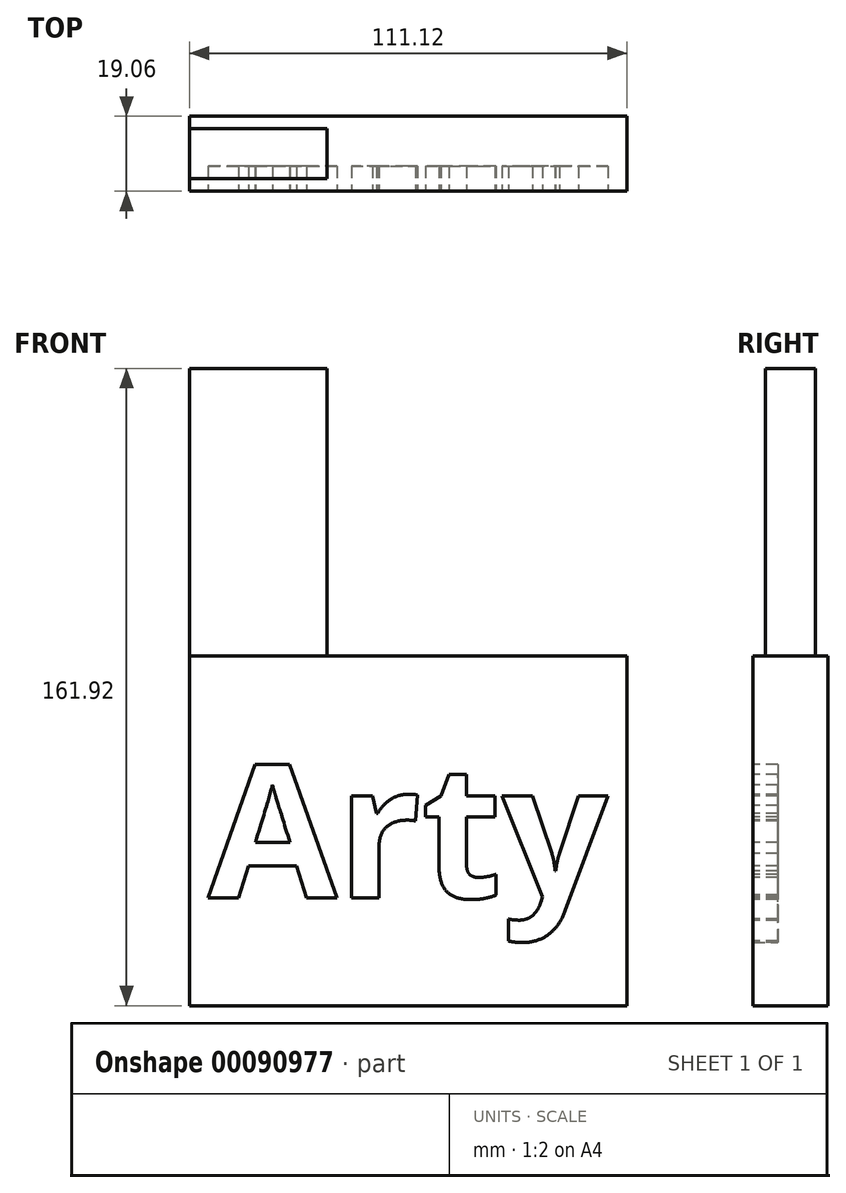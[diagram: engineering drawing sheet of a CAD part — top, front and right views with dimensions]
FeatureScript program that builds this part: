
annotation { "Feature Type Name" : "Feature", "Feature Type Description" : "" }
export const myFeature = defineFeature(function(context is Context, id is Id, definition is map)
    precondition{}
    {
        {
            var Q0;
            Q0=qCreatedBy(makeId("Front.planeOp"),FACE);
            var sketch = newSketch(context, id + "F0", { "sketchPlane" : qUnion([Q0])});
            skLineSegment(sketch, "E0.bottom", {"start": v(55.56, 44.45) * mm, "end": v(-55.56, 44.45) * mm});
            skLineSegment(sketch, "E0.top", {"start": v(55.56, -44.45) * mm, "end": v(-55.56, -44.45) * mm});
            skLineSegment(sketch, "E0.left", {"start": v(55.56, 44.45) * mm, "end": v(55.56, -44.45) * mm});
            skLineSegment(sketch, "E0.right", {"start": v(-55.56, 44.45) * mm, "end": v(-55.56, -44.45) * mm});
            skPoint(sketch, "E0.middle", {"position": v(0, 0) * mm});
            skSolve(sketch);
        }
        {
            var Q0;
            Q0=makeQuery(id+"F0.imprint","IMPRINT",FACE,{"disambiguationData":[TD([[makeQuery(id+"F0.imprint","IMPRINT",EDGE,{"derivedFrom":sQuery(id+"F0.wireOp",EDGE,"E0.bottom")}),1.0]])]});
            extrude(context, id + "F1", {"entities" : qUnion([Q0]), "endBound" : BoundingType.SYMMETRIC, "depth" : 19.05 * mm});
        }
        {
            var Q0;
            Q0=qCreatedBy(makeId("Front.planeOp"),FACE);
            var sketch = newSketch(context, id + "F2", { "sketchPlane" : qUnion([Q0])});
            skLineSegment(sketch, "E1.bottom", {"start": v(-55.56, 44.45) * mm, "end": v(-20.64, 44.45) * mm});
            skLineSegment(sketch, "E1.top", {"start": v(-55.56, 117.48) * mm, "end": v(-20.64, 117.48) * mm});
            skLineSegment(sketch, "E1.left", {"start": v(-55.56, 44.45) * mm, "end": v(-55.56, 117.48) * mm});
            skLineSegment(sketch, "E1.right", {"start": v(-20.64, 44.45) * mm, "end": v(-20.64, 117.48) * mm});
            skSolve(sketch);
        }
        {
            var Q0;
            Q0 = qSketchRegion(id + "F2", true);
            extrude(context, id + "F3", {"entities" : qUnion([Q0]), "operationType" : NewBodyOperationType.ADD, "endBound" : BoundingType.SYMMETRIC, "depth" : 12.7 * mm});
        }
        {
            var Q0;
            Q0=makeQuery(id+"F1.opExtrude","CAP_FACE",FACE,{"disambiguationData":[OSD([sQuery(id+"F0.wireOp",EDGE,"E0.bottom"),sQuery(id+"F0.wireOp",EDGE,"E0.top"),sQuery(id+"F0.wireOp",EDGE,"E0.left"),sQuery(id+"F0.wireOp",EDGE,"E0.right")])],"isStart":false});
            var sketch = newSketch(context, id + "F4", { "sketchPlane" : qUnion([Q0])});
            skText(sketch, "E2", { "text": "Arty", "fontName": "OpenSans-Bold.ttf"});
            const initialGuessF4  = {"E2": [-0.0508, -0.01704, 1, 0, 0.03407]};
            skSetInitialGuess(sketch, initialGuessF4);
            skSolve(sketch);
        }
        {
            var Q0;
            Q0 = qSketchRegion(id + "F4", true);
            extrude(context, id + "F5", {"entities" : qUnion([Q0]), "operationType" : NewBodyOperationType.REMOVE, "oppositeDirection" : true, "depth" : 6.35 * mm});
        }
    });
